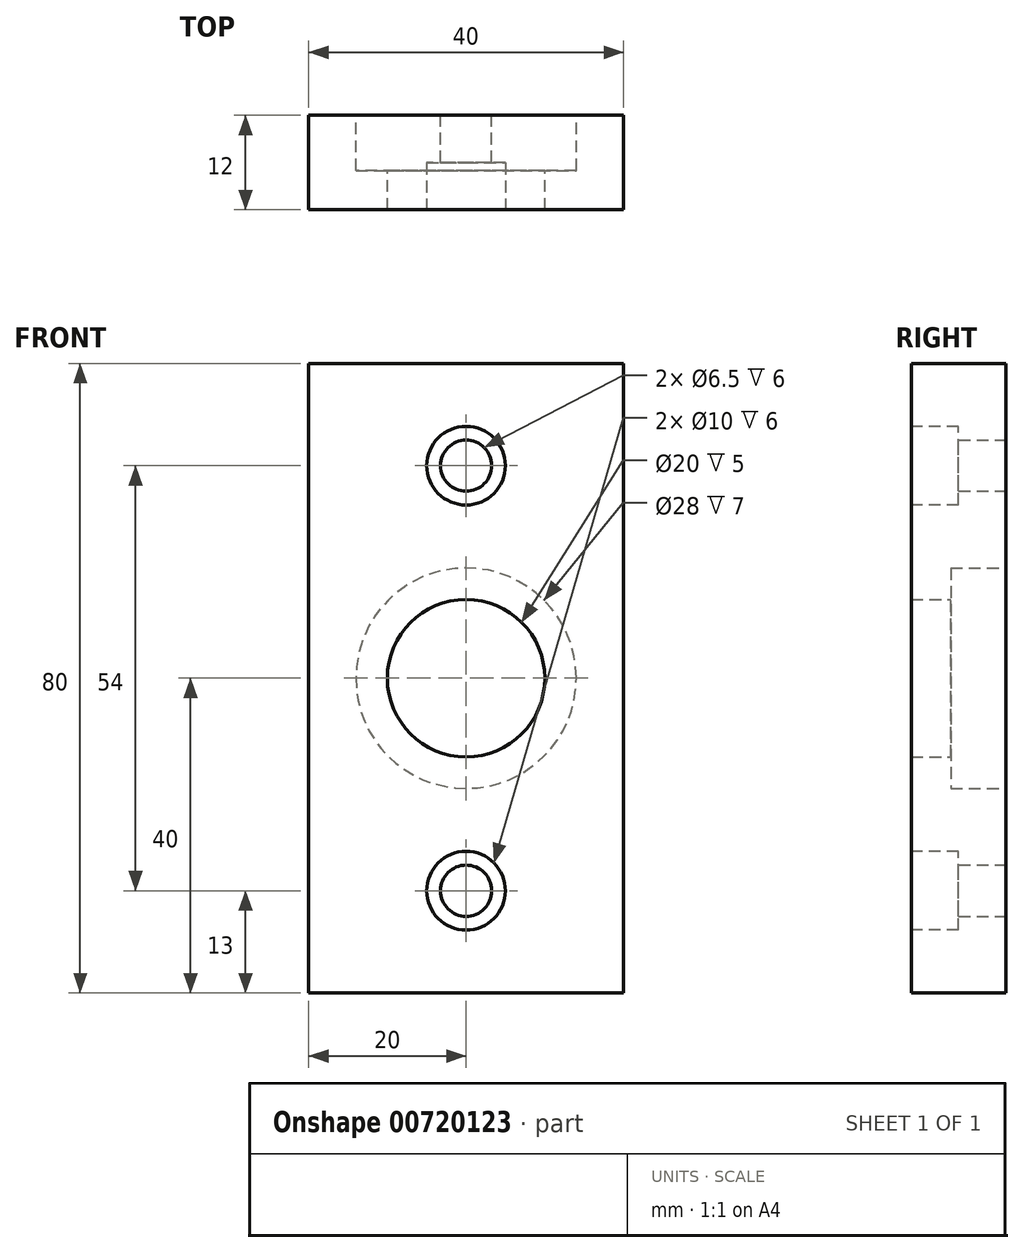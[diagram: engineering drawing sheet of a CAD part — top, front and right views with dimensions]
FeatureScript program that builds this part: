
annotation { "Feature Type Name" : "Feature", "Feature Type Description" : "" }
export const myFeature = defineFeature(function(context is Context, id is Id, definition is map)
    precondition{}
    {
        {
            var Q0;
            Q0=qCreatedBy(makeId("Front.planeOp"),FACE);
            var sketch = newSketch(context, id + "F0", { "sketchPlane" : qUnion([Q0])});
            skLineSegment(sketch, "E0.bottom", {"start": v(0, 0) * mm, "end": v(40, 0) * mm});
            skLineSegment(sketch, "E0.top", {"start": v(0, 80) * mm, "end": v(40, 80) * mm});
            skLineSegment(sketch, "E0.left", {"start": v(0, 0) * mm, "end": v(0, 80) * mm});
            skLineSegment(sketch, "E0.right", {"start": v(40, 0) * mm, "end": v(40, 80) * mm});
            skCircle(sketch, "E1", {"center": v(20, 40) * mm, "radius": 10 * mm});
            skPoint(sketch, "E1.centerSnap0", {"position": v(20, 80) * mm});
            skPoint(sketch, "E1.centerSnap1", {"position": v(0, 40) * mm});
            skCircle(sketch, "E2", {"center": v(20, 13) * mm, "radius": 3.25 * mm});
            skPoint(sketch, "E2.centerSnap0", {"position": v(20, 0) * mm});
            skCircle(sketch, "E3", {"center": v(20, 67) * mm, "radius": 3.25 * mm});
            skSolve(sketch);
        }
        {
            var Q0;
            Q0=makeQuery(id+"F0.imprint","IMPRINT",FACE,{"disambiguationData":[TD([[makeQuery(id+"F0.imprint","IMPRINT",EDGE,{"derivedFrom":sQuery(id+"F0.wireOp",EDGE,"E0.bottom")}),1.0]])]});
            extrude(context, id + "F1", {"entities" : qUnion([Q0]), "depth" : 12 * mm, "offsetDistance" : 25 * mm});
        }
        {
            var Q0;
            Q0=makeQuery(id+"F1.opExtrude","CAP_FACE",FACE,{"disambiguationData":[OSD([sQuery(id+"F0.wireOp",EDGE,"E0.bottom"),sQuery(id+"F0.wireOp",EDGE,"E0.top"),sQuery(id+"F0.wireOp",EDGE,"E0.left"),sQuery(id+"F0.wireOp",EDGE,"E0.right"),sQuery(id+"F0.wireOp",EDGE,"E1"),sQuery(id+"F0.wireOp",EDGE,"E2"),sQuery(id+"F0.wireOp",EDGE,"E3"),sQuery(id+"F0.wireOp",EDGE,"LHpxsSz5-eAHS-cZ5K-flmr-d181EowS3kwZ"),sQuery(id+"F0.wireOp",EDGE,"bf2VshPH-9uiV-psqV-xKke-R7FIbc3S2vTj")])],"isStart":false});
            var sketch = newSketch(context, id + "F2", { "sketchPlane" : qUnion([Q0])});
            skCircle(sketch, "E4", {"center": v(20, 67) * mm, "radius": 5 * mm});
            skCircle(sketch, "E5", {"center": v(20, 13) * mm, "radius": 5 * mm});
            skSolve(sketch);
        }
        {
            var Q0;
            Q0=qSketchRegion(id+"F2",true);
            extrude(context, id + "F3", {"entities" : qUnion([Q0]), "operationType" : NewBodyOperationType.REMOVE, "oppositeDirection" : true, "depth" : 6 * mm, "offsetDistance" : 25 * mm});
        }
        {
            var Q0;
            Q0=makeQuery(id+"F1.opExtrude","CAP_FACE",FACE,{"disambiguationData":[OSD([sQuery(id+"F0.wireOp",EDGE,"E0.bottom"),sQuery(id+"F0.wireOp",EDGE,"E0.top"),sQuery(id+"F0.wireOp",EDGE,"E0.left"),sQuery(id+"F0.wireOp",EDGE,"E0.right"),sQuery(id+"F0.wireOp",EDGE,"E1"),sQuery(id+"F0.wireOp",EDGE,"E2"),sQuery(id+"F0.wireOp",EDGE,"E3"),sQuery(id+"F0.wireOp",EDGE,"LHpxsSz5-eAHS-cZ5K-flmr-d181EowS3kwZ"),sQuery(id+"F0.wireOp",EDGE,"bf2VshPH-9uiV-psqV-xKke-R7FIbc3S2vTj")])],"isStart":true});
            var sketch = newSketch(context, id + "F4", { "sketchPlane" : qUnion([Q0])});
            skCircle(sketch, "E6", {"center": v(-20, 40) * mm, "radius": 14 * mm});
            skSolve(sketch);
        }
        {
            var Q0;
            Q0=makeQuery(id+"F4.imprint","IMPRINT",FACE,{"disambiguationData":[TD([[makeQuery(id+"F4.imprint","IMPRINT",EDGE,{"derivedFrom":sQuery(id+"F4.wireOp",EDGE,"E6")}),1.0]])]});
            extrude(context, id + "F5", {"entities" : qUnion([Q0]), "operationType" : NewBodyOperationType.REMOVE, "oppositeDirection" : true, "depth" : 7 * mm, "offsetDistance" : 25 * mm});
        }
    });
